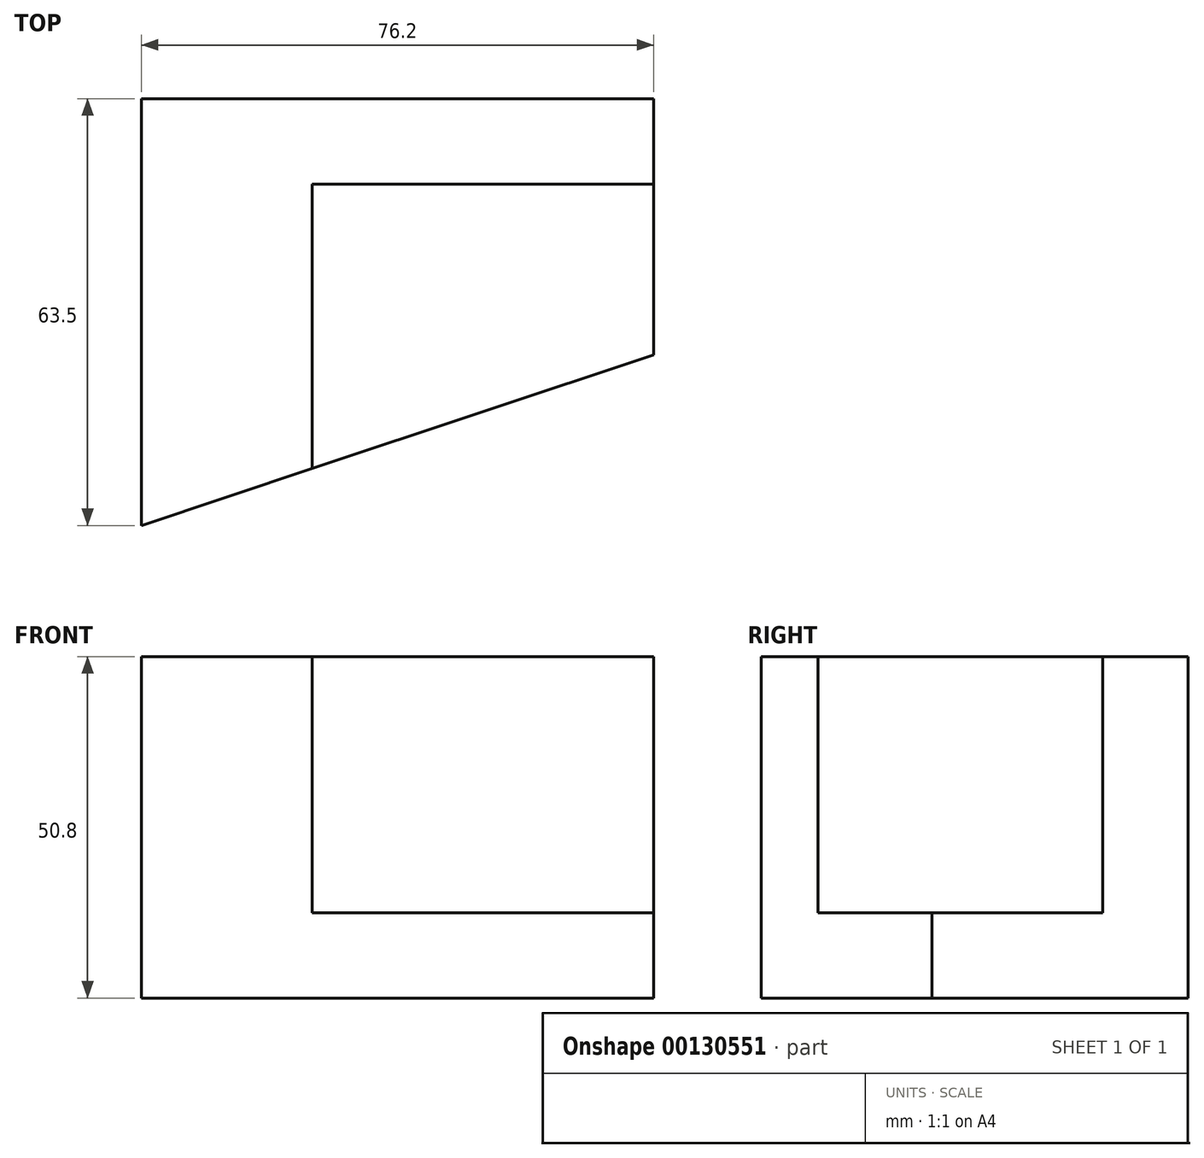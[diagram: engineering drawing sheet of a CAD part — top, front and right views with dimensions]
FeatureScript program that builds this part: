
annotation { "Feature Type Name" : "Feature", "Feature Type Description" : "" }
export const myFeature = defineFeature(function(context is Context, id is Id, definition is map)
    precondition{}
    {
        {
            var Q0;
            Q0=qCreatedBy(makeId("Top.planeOp"),FACE);
            var sketch = newSketch(context, id + "F0", { "sketchPlane" : qUnion([Q0])});
            skLineSegment(sketch, "E0", {"start": v(0, 0) * mm, "end": v(76.2, 0) * mm});
            skLineSegment(sketch, "E1", {"start": v(76.2, 0) * mm, "end": v(76.2, -38.1) * mm});
            skLineSegment(sketch, "E2", {"start": v(76.2, -38.1) * mm, "end": v(0, -63.5) * mm});
            skLineSegment(sketch, "E3", {"start": v(0, -63.5) * mm, "end": v(0, 0) * mm});
            skSolve(sketch);
        }
        {
            var Q0;
            Q0 = qSketchRegion(id + "F0", true);
            extrude(context, id + "F1", {"entities" : qUnion([Q0]), "depth" : 12.7 * mm});
        }
        {
            var Q0;
            Q0=makeQuery(id+"F1.opExtrude","CAP_FACE",FACE,{"disambiguationData":[OSD([sQuery(id+"F0.wireOp",EDGE,"E0"),sQuery(id+"F0.wireOp",EDGE,"E1"),sQuery(id+"F0.wireOp",EDGE,"E2"),sQuery(id+"F0.wireOp",EDGE,"E3")])],"isStart":false});
            var sketch = newSketch(context, id + "F2", { "sketchPlane" : qUnion([Q0])});
            skLineSegment(sketch, "E4", {"start": v(76.2, 0) * mm, "end": v(0, 0) * mm});
            skLineSegment(sketch, "E5", {"start": v(0, 0) * mm, "end": v(0, -63.5) * mm});
            skLineSegment(sketch, "E6", {"start": v(0, -63.5) * mm, "end": v(25.4, -55.03) * mm});
            skLineSegment(sketch, "E7", {"start": v(25.4, -55.03) * mm, "end": v(25.4, -12.7) * mm});
            skLineSegment(sketch, "E8", {"start": v(25.4, -12.7) * mm, "end": v(76.2, -12.7) * mm});
            skLineSegment(sketch, "E9", {"start": v(76.2, -12.7) * mm, "end": v(76.2, 0) * mm});
            skSolve(sketch);
        }
        {
            var Q0;
            Q0 = qSketchRegion(id + "F2", true);
            extrude(context, id + "F3", {"entities" : qUnion([Q0]), "operationType" : NewBodyOperationType.ADD, "depth" : 38.1 * mm});
        }
    });
